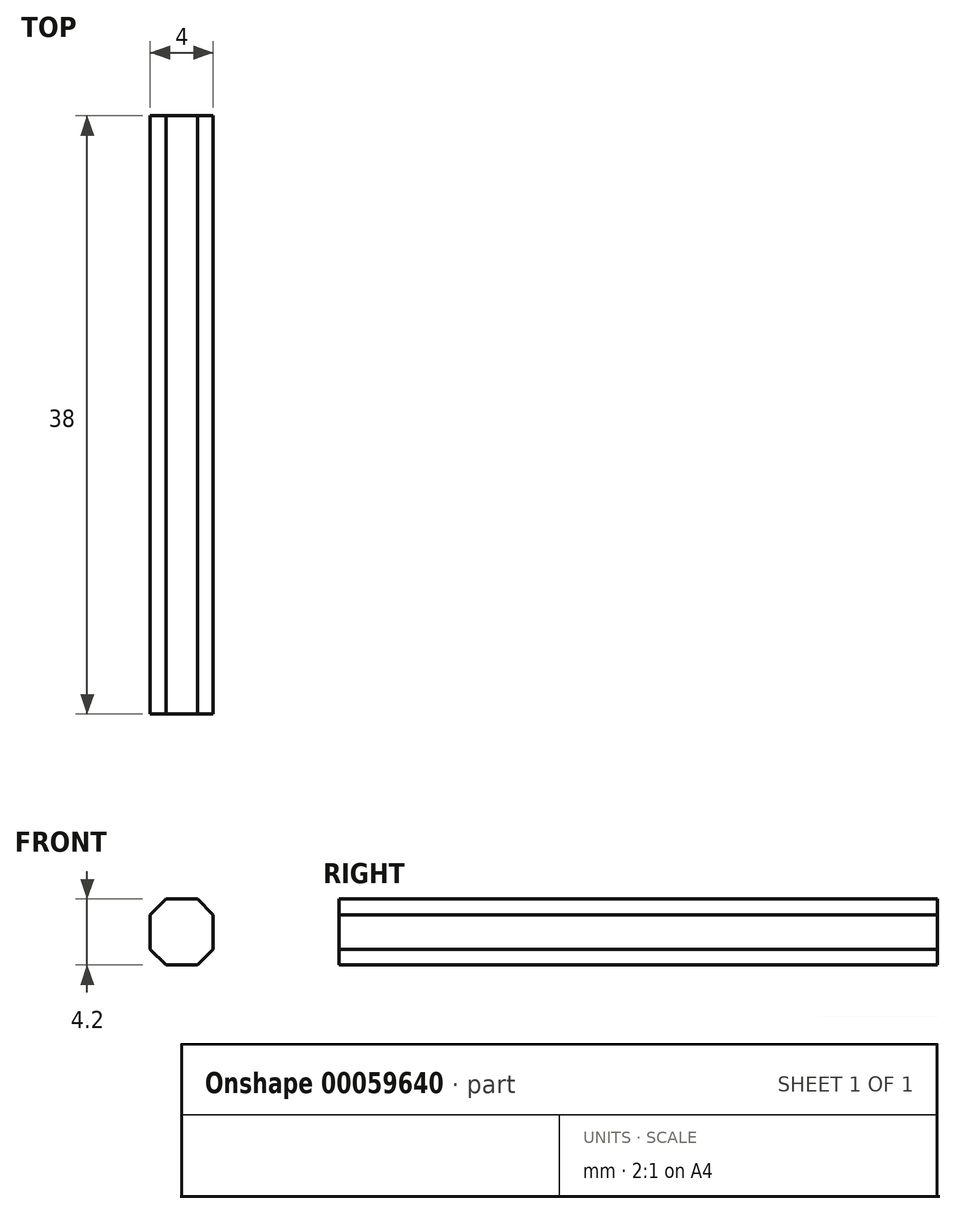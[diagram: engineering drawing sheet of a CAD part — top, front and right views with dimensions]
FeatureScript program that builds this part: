
annotation { "Feature Type Name" : "Feature", "Feature Type Description" : "" }
export const myFeature = defineFeature(function(context is Context, id is Id, definition is map)
    precondition{}
    {
        {
            var Q0;
            Q0=qCreatedBy(makeId("Front.planeOp"),FACE);
            var sketch = newSketch(context, id + "F0", { "sketchPlane" : qUnion([Q0])});
            skLineSegment(sketch, "E0.rect.bottom", {"start": v(-2, 2.1) * mm, "end": v(2, 2.1) * mm});
            skLineSegment(sketch, "E0.rect.top", {"start": v(-2, -2.1) * mm, "end": v(2, -2.1) * mm});
            skLineSegment(sketch, "E0.rect.left", {"start": v(-2, 2.1) * mm, "end": v(-2, -2.1) * mm});
            skLineSegment(sketch, "E0.rect.right", {"start": v(2, 2.1) * mm, "end": v(2, -2.1) * mm});
            skPoint(sketch, "E0.rect.middle", {"position": v(0, 0) * mm});
            skSolve(sketch);
        }
        {
            var Q0;
            Q0=makeQuery(id+"F0.imprint","IMPRINT",FACE,{"disambiguationData":[TD([[makeQuery(id+"F0.imprint","IMPRINT",EDGE,{"derivedFrom":sQuery(id+"F0.wireOp",EDGE,"E0.rect.bottom")}),-1.0]])]});
            extrude(context, id + "F1", {"entities" : qUnion([Q0]), "depth" : 38 * mm});
        }
        {
            var Q0;
            Q0=makeQuery(id+"F1.opExtrude","SWEPT_EDGE",EDGE,{"disambiguationData":[OSD([sQuery(id+"F0.wireOp",EDGE,"E0.rect.top"),sQuery(id+"F0.wireOp",EDGE,"E0.rect.left")])]});
            var Q1;
            Q1=makeQuery(id+"F1.opExtrude","SWEPT_EDGE",EDGE,{"disambiguationData":[OSD([sQuery(id+"F0.wireOp",EDGE,"E0.rect.bottom"),sQuery(id+"F0.wireOp",EDGE,"E0.rect.left")])]});
            var Q2;
            Q2=makeQuery(id+"F1.opExtrude","SWEPT_EDGE",EDGE,{"disambiguationData":[OSD([sQuery(id+"F0.wireOp",EDGE,"E0.rect.bottom"),sQuery(id+"F0.wireOp",EDGE,"E0.rect.right")])]});
            var Q3;
            Q3=makeQuery(id+"F1.opExtrude","SWEPT_EDGE",EDGE,{"disambiguationData":[OSD([sQuery(id+"F0.wireOp",EDGE,"E0.rect.top"),sQuery(id+"F0.wireOp",EDGE,"E0.rect.right")])]});
            chamfer(context, id + "F2", {"entities" : qUnion([Q0, Q1, Q2, Q3]), "width" : 1 * mm, "tangentPropagation" : true});
        }
    });
